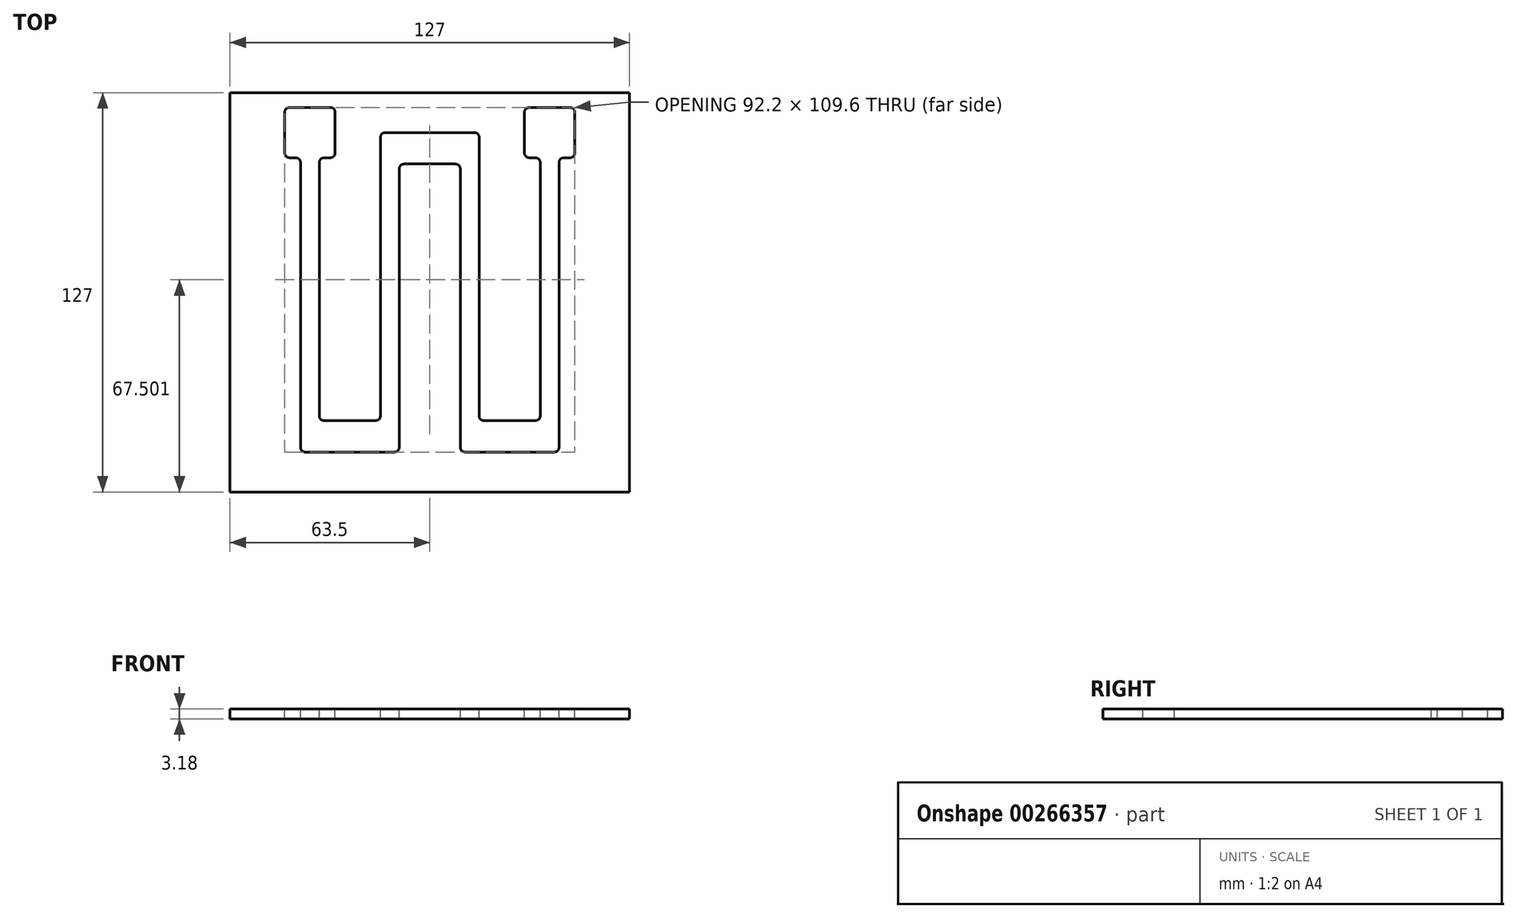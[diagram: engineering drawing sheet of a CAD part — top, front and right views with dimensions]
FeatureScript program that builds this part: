
annotation { "Feature Type Name" : "Feature", "Feature Type Description" : "" }
export const myFeature = defineFeature(function(context is Context, id is Id, definition is map)
    precondition{}
    {
        {
            var Q0;
            Q0=qCreatedBy(makeId("Front.planeOp"),FACE);
            var sketch = newSketch(context, id + "F0", { "sketchPlane" : qUnion([Q0])});
            skLineSegment(sketch, "E0.bottom", {"start": v(0, 0) * mm, "end": v(127, 0) * mm});
            skLineSegment(sketch, "E0.top", {"start": v(0, 3.18) * mm, "end": v(127, 3.18) * mm});
            skLineSegment(sketch, "E0.left", {"start": v(0, 0) * mm, "end": v(0, 3.18) * mm});
            skLineSegment(sketch, "E0.right", {"start": v(127, 0) * mm, "end": v(127, 3.18) * mm});
            skSolve(sketch);
        }
        {
            var Q0;
            Q0=makeQuery(id+"F0.imprint","IMPRINT",FACE,{"disambiguationData":[TD([[makeQuery(id+"F0.imprint","IMPRINT",EDGE,{"derivedFrom":sQuery(id+"F0.wireOp",EDGE,"E0.bottom")}),1.0]])]});
            extrude(context, id + "F1", {"entities" : qUnion([Q0]), "oppositeDirection" : true, "depth" : 127 * mm});
        }
        {
            var Q0;
            Q0=makeQuery(id+"F1.opExtrude","SWEPT_FACE",FACE,{"disambiguationData":[OSD([sQuery(id+"F0.wireOp",EDGE,"E0.top")])]});
            var sketch = newSketch(context, id + "F2", { "sketchPlane" : qUnion([Q0])});
            skPoint(sketch, "E1", {"position": v(25.4, 114.3) * mm});
            skPoint(sketch, "E2", {"position": v(101.6, 114.3) * mm});
            skLineSegment(sketch, "E3.bottom", {"start": v(33.4, 122.3) * mm, "end": v(17.4, 122.3) * mm});
            skLineSegment(sketch, "E3.top", {"start": v(33.4, 106.3) * mm, "end": v(28.4, 106.3) * mm});
            skLineSegment(sketch, "E3.left", {"start": v(33.4, 122.3) * mm, "end": v(33.4, 106.3) * mm});
            skLineSegment(sketch, "E3.right", {"start": v(17.4, 122.3) * mm, "end": v(17.4, 106.3) * mm});
            skLineSegment(sketch, "E4.bottom", {"start": v(109.6, 122.3) * mm, "end": v(93.6, 122.3) * mm});
            skLineSegment(sketch, "E4.top", {"start": v(109.6, 106.3) * mm, "end": v(101.6, 106.3) * mm});
            skLineSegment(sketch, "E4.left", {"start": v(109.6, 122.3) * mm, "end": v(109.6, 106.3) * mm});
            skLineSegment(sketch, "E4.right", {"start": v(93.6, 122.3) * mm, "end": v(93.6, 106.3) * mm});
            skLineSegment(sketch, "E5", {"start": v(25.4, 114.3) * mm, "end": v(25.4, 12.7) * mm, "construction": true});
            skLineSegment(sketch, "E6", {"start": v(25.4, 12.7) * mm, "end": v(50.8, 12.7) * mm, "construction": true});
            skLineSegment(sketch, "E7", {"start": v(50.8, 12.7) * mm, "end": v(50.8, 114.3) * mm, "construction": true});
            skLineSegment(sketch, "E8", {"start": v(50.8, 114.3) * mm, "end": v(76.2, 114.3) * mm, "construction": true});
            skLineSegment(sketch, "E9", {"start": v(76.2, 114.3) * mm, "end": v(76.2, 12.7) * mm, "construction": true});
            skLineSegment(sketch, "E10", {"start": v(76.2, 12.7) * mm, "end": v(101.6, 12.7) * mm, "construction": true});
            skLineSegment(sketch, "E11", {"start": v(101.6, 12.7) * mm, "end": v(101.6, 114.3) * mm, "construction": true});
            skLineSegment(sketch, "E12.top", {"start": v(28.4, 12.7) * mm, "end": v(22.4, 12.7) * mm});
            skLineSegment(sketch, "E12.left", {"start": v(28.4, 106.3) * mm, "end": v(28.4, 22.7) * mm});
            skLineSegment(sketch, "E12.right", {"start": v(22.4, 106.3) * mm, "end": v(22.4, 12.7) * mm});
            skPoint(sketch, "E12.middle", {"position": v(25.4, 63.5) * mm});
            skLineSegment(sketch, "E13.bottom", {"start": v(53.8, 114.3) * mm, "end": v(47.8, 114.3) * mm});
            skLineSegment(sketch, "E13.top", {"start": v(53.8, 12.7) * mm, "end": v(47.8, 12.7) * mm});
            skLineSegment(sketch, "E13.left", {"start": v(53.8, 104.3) * mm, "end": v(53.8, 12.7) * mm});
            skLineSegment(sketch, "E13.right", {"start": v(47.8, 114.3) * mm, "end": v(47.8, 22.7) * mm});
            skPoint(sketch, "E13.middle", {"position": v(50.8, 63.5) * mm});
            skLineSegment(sketch, "E14.bottom", {"start": v(79.2, 114.3) * mm, "end": v(73.2, 114.3) * mm});
            skLineSegment(sketch, "E14.top", {"start": v(79.2, 12.7) * mm, "end": v(73.2, 12.7) * mm});
            skLineSegment(sketch, "E14.left", {"start": v(79.2, 114.3) * mm, "end": v(79.2, 22.7) * mm});
            skLineSegment(sketch, "E14.right", {"start": v(73.2, 104.3) * mm, "end": v(73.2, 12.7) * mm});
            skPoint(sketch, "E14.middle", {"position": v(76.2, 63.5) * mm});
            skLineSegment(sketch, "E15.top", {"start": v(104.6, 12.7) * mm, "end": v(98.6, 12.7) * mm});
            skLineSegment(sketch, "E15.left", {"start": v(104.6, 106.3) * mm, "end": v(104.6, 12.7) * mm});
            skLineSegment(sketch, "E15.right", {"start": v(98.6, 106.3) * mm, "end": v(98.6, 22.7) * mm});
            skPoint(sketch, "E15.middle", {"position": v(101.6, 63.5) * mm});
            skLineSegment(sketch, "E16", {"start": v(22.4, 12.7) * mm, "end": v(53.8, 12.7) * mm});
            skLineSegment(sketch, "E17", {"start": v(73.2, 12.7) * mm, "end": v(104.6, 12.7) * mm});
            skLineSegment(sketch, "E18", {"start": v(47.8, 114.3) * mm, "end": v(79.2, 114.3) * mm});
            skLineSegment(sketch, "E19", {"start": v(28.4, 22.7) * mm, "end": v(47.8, 22.7) * mm});
            skLineSegment(sketch, "E20", {"start": v(79.2, 22.7) * mm, "end": v(98.6, 22.7) * mm});
            skLineSegment(sketch, "E21", {"start": v(53.8, 104.3) * mm, "end": v(73.2, 104.3) * mm});
            skLineSegment(sketch, "E22.trimOffspring", {"start": v(22.4, 106.3) * mm, "end": v(17.4, 106.3) * mm});
            skPoint(sketch, "E23.orphan", {"position": v(22.4, 114.3) * mm});
            skPoint(sketch, "E12.bottom.start.orphan", {"position": v(28.4, 114.3) * mm});
            skLineSegment(sketch, "E24.trimOffspring", {"start": v(98.6, 106.3) * mm, "end": v(93.6, 106.3) * mm});
            skPoint(sketch, "E25.orphan", {"position": v(104.6, 114.3) * mm});
            skPoint(sketch, "E26.orphan", {"position": v(98.6, 114.3) * mm});
            skSolve(sketch);
        }
        {
            var Q0;
            Q0=makeQuery(id+"F2.imprint","IMPRINT",FACE,{"disambiguationData":[TD([[makeQuery(id+"F2.imprint","IMPRINT",EDGE,{"derivedFrom":sQuery(id+"F2.wireOp",EDGE,"E3.bottom")}),1.0]])]});
            extrude(context, id + "F3", {"entities" : qUnion([Q0]), "operationType" : NewBodyOperationType.REMOVE, "oppositeDirection" : true, "depth" : 25 * mm});
        }
        {
            var Q0;
            Q0=makeQuery(id+"F3.boolean.opBoolean","COPY",EDGE,{"derivedFrom":makeQuery(id+"F3.opExtrude","SWEPT_EDGE",EDGE,{"disambiguationData":[OSD([sQuery(id+"F2.wireOp",EDGE,"E3.bottom"),sQuery(id+"F2.wireOp",EDGE,"E3.right")])]})});
            var Q1;
            Q1=makeQuery(id+"F3.boolean.opBoolean","COPY",EDGE,{"derivedFrom":makeQuery(id+"F3.opExtrude","SWEPT_EDGE",EDGE,{"disambiguationData":[OSD([sQuery(id+"F2.wireOp",EDGE,"E3.bottom"),sQuery(id+"F2.wireOp",EDGE,"E3.left")])]})});
            var Q2;
            Q2=makeQuery(id+"F3.boolean.opBoolean","COPY",EDGE,{"derivedFrom":makeQuery(id+"F3.opExtrude","SWEPT_EDGE",EDGE,{"disambiguationData":[OSD([sQuery(id+"F2.wireOp",EDGE,"E3.right"),sQuery(id+"F2.wireOp",EDGE,"E22.trimOffspring")])]})});
            var Q3;
            Q3=makeQuery(id+"F3.boolean.opBoolean","COPY",EDGE,{"derivedFrom":makeQuery(id+"F3.opExtrude","SWEPT_EDGE",EDGE,{"disambiguationData":[OSD([sQuery(id+"F2.wireOp",EDGE,"E12.right"),sQuery(id+"F2.wireOp",EDGE,"E22.trimOffspring")])]})});
            var Q4;
            Q4=makeQuery(id+"F3.boolean.opBoolean","COPY",EDGE,{"derivedFrom":makeQuery(id+"F3.opExtrude","SWEPT_EDGE",EDGE,{"disambiguationData":[OSD([sQuery(id+"F2.wireOp",EDGE,"E3.top"),sQuery(id+"F2.wireOp",EDGE,"E12.left")])]})});
            var Q5;
            Q5=makeQuery(id+"F3.boolean.opBoolean","COPY",EDGE,{"derivedFrom":makeQuery(id+"F3.opExtrude","SWEPT_EDGE",EDGE,{"disambiguationData":[OSD([sQuery(id+"F2.wireOp",EDGE,"E3.top"),sQuery(id+"F2.wireOp",EDGE,"E3.left")])]})});
            var Q6;
            Q6=makeQuery(id+"F3.boolean.opBoolean","COPY",EDGE,{"derivedFrom":makeQuery(id+"F3.opExtrude","SWEPT_EDGE",EDGE,{"disambiguationData":[OSD([sQuery(id+"F2.wireOp",EDGE,"E13.left"),sQuery(id+"F2.wireOp",EDGE,"E21")])]})});
            var Q7;
            Q7=makeQuery(id+"F3.boolean.opBoolean","COPY",EDGE,{"derivedFrom":makeQuery(id+"F3.opExtrude","SWEPT_EDGE",EDGE,{"disambiguationData":[OSD([sQuery(id+"F2.wireOp",EDGE,"E14.right"),sQuery(id+"F2.wireOp",EDGE,"E21")])]})});
            var Q8;
            Q8=makeQuery(id+"F3.boolean.opBoolean","COPY",EDGE,{"derivedFrom":makeQuery(id+"F3.opExtrude","SWEPT_EDGE",EDGE,{"disambiguationData":[OSD([sQuery(id+"F2.wireOp",EDGE,"E15.right"),sQuery(id+"F2.wireOp",EDGE,"E24.trimOffspring")])]})});
            var Q9;
            Q9=makeQuery(id+"F3.boolean.opBoolean","COPY",EDGE,{"derivedFrom":makeQuery(id+"F3.opExtrude","SWEPT_EDGE",EDGE,{"disambiguationData":[OSD([sQuery(id+"F2.wireOp",EDGE,"E4.top"),sQuery(id+"F2.wireOp",EDGE,"E15.left")])]})});
            var Q10;
            Q10=makeQuery(id+"F3.boolean.opBoolean","COPY",EDGE,{"derivedFrom":makeQuery(id+"F3.opExtrude","SWEPT_EDGE",EDGE,{"disambiguationData":[OSD([sQuery(id+"F2.wireOp",EDGE,"E15.left"),sQuery(id+"F2.wireOp",EDGE,"E17")])]})});
            var Q11;
            Q11=makeQuery(id+"F3.boolean.opBoolean","COPY",EDGE,{"derivedFrom":makeQuery(id+"F3.opExtrude","SWEPT_EDGE",EDGE,{"disambiguationData":[OSD([sQuery(id+"F2.wireOp",EDGE,"E14.left"),sQuery(id+"F2.wireOp",EDGE,"E20")])]})});
            var Q12;
            Q12=makeQuery(id+"F3.boolean.opBoolean","COPY",EDGE,{"derivedFrom":makeQuery(id+"F3.opExtrude","SWEPT_EDGE",EDGE,{"disambiguationData":[OSD([sQuery(id+"F2.wireOp",EDGE,"E12.left"),sQuery(id+"F2.wireOp",EDGE,"E19")])]})});
            var Q13;
            Q13=makeQuery(id+"F3.boolean.opBoolean","COPY",EDGE,{"derivedFrom":makeQuery(id+"F3.opExtrude","SWEPT_EDGE",EDGE,{"disambiguationData":[OSD([sQuery(id+"F2.wireOp",EDGE,"E13.left"),sQuery(id+"F2.wireOp",EDGE,"E16")])]})});
            var Q14;
            Q14=makeQuery(id+"F3.boolean.opBoolean","COPY",EDGE,{"derivedFrom":makeQuery(id+"F3.opExtrude","SWEPT_EDGE",EDGE,{"disambiguationData":[OSD([sQuery(id+"F2.wireOp",EDGE,"E13.right"),sQuery(id+"F2.wireOp",EDGE,"E19")])]})});
            var Q15;
            Q15=makeQuery(id+"F3.boolean.opBoolean","COPY",EDGE,{"derivedFrom":makeQuery(id+"F3.opExtrude","SWEPT_EDGE",EDGE,{"disambiguationData":[OSD([sQuery(id+"F2.wireOp",EDGE,"E15.right"),sQuery(id+"F2.wireOp",EDGE,"E20")])]})});
            var Q16;
            Q16=makeQuery(id+"F3.boolean.opBoolean","COPY",EDGE,{"derivedFrom":makeQuery(id+"F3.opExtrude","SWEPT_EDGE",EDGE,{"disambiguationData":[OSD([sQuery(id+"F2.wireOp",EDGE,"E14.right"),sQuery(id+"F2.wireOp",EDGE,"E17")])]})});
            var Q17;
            Q17=makeQuery(id+"F3.boolean.opBoolean","COPY",EDGE,{"derivedFrom":makeQuery(id+"F3.opExtrude","SWEPT_EDGE",EDGE,{"disambiguationData":[OSD([sQuery(id+"F2.wireOp",EDGE,"E12.right"),sQuery(id+"F2.wireOp",EDGE,"E16")])]})});
            var Q18;
            Q18=makeQuery(id+"F3.boolean.opBoolean","COPY",EDGE,{"derivedFrom":makeQuery(id+"F3.opExtrude","SWEPT_EDGE",EDGE,{"disambiguationData":[OSD([sQuery(id+"F2.wireOp",EDGE,"E4.bottom"),sQuery(id+"F2.wireOp",EDGE,"E4.left")])]})});
            var Q19;
            Q19=makeQuery(id+"F3.boolean.opBoolean","COPY",EDGE,{"derivedFrom":makeQuery(id+"F3.opExtrude","SWEPT_EDGE",EDGE,{"disambiguationData":[OSD([sQuery(id+"F2.wireOp",EDGE,"E14.left"),sQuery(id+"F2.wireOp",EDGE,"E18")])]})});
            var Q20;
            Q20=makeQuery(id+"F3.boolean.opBoolean","COPY",EDGE,{"derivedFrom":makeQuery(id+"F3.opExtrude","SWEPT_EDGE",EDGE,{"disambiguationData":[OSD([sQuery(id+"F2.wireOp",EDGE,"E13.right"),sQuery(id+"F2.wireOp",EDGE,"E18")])]})});
            var Q21;
            Q21=makeQuery(id+"F3.boolean.opBoolean","COPY",EDGE,{"derivedFrom":makeQuery(id+"F3.opExtrude","SWEPT_EDGE",EDGE,{"disambiguationData":[OSD([sQuery(id+"F2.wireOp",EDGE,"E4.bottom"),sQuery(id+"F2.wireOp",EDGE,"E4.right")])]})});
            var Q22;
            Q22=makeQuery(id+"F3.boolean.opBoolean","COPY",EDGE,{"derivedFrom":makeQuery(id+"F3.opExtrude","SWEPT_EDGE",EDGE,{"disambiguationData":[OSD([sQuery(id+"F2.wireOp",EDGE,"E4.top"),sQuery(id+"F2.wireOp",EDGE,"E4.left")])]})});
            var Q23;
            Q23=makeQuery(id+"F3.boolean.opBoolean","COPY",EDGE,{"derivedFrom":makeQuery(id+"F3.opExtrude","SWEPT_EDGE",EDGE,{"disambiguationData":[OSD([sQuery(id+"F2.wireOp",EDGE,"E4.right"),sQuery(id+"F2.wireOp",EDGE,"E24.trimOffspring")])]})});
            fillet(context, id + "F4", {"entities" : qUnion([Q0, Q1, Q2, Q3, Q4, Q5, Q6, Q7, Q8, Q9, Q10, Q11, Q12, Q13, Q14, Q15, Q16, Q17, Q18, Q19, Q20, Q21, Q22, Q23]), "radius" : 1.5 * mm, "tangentPropagation" : true, "allowEdgeOverflow" : false});
        }
    });
